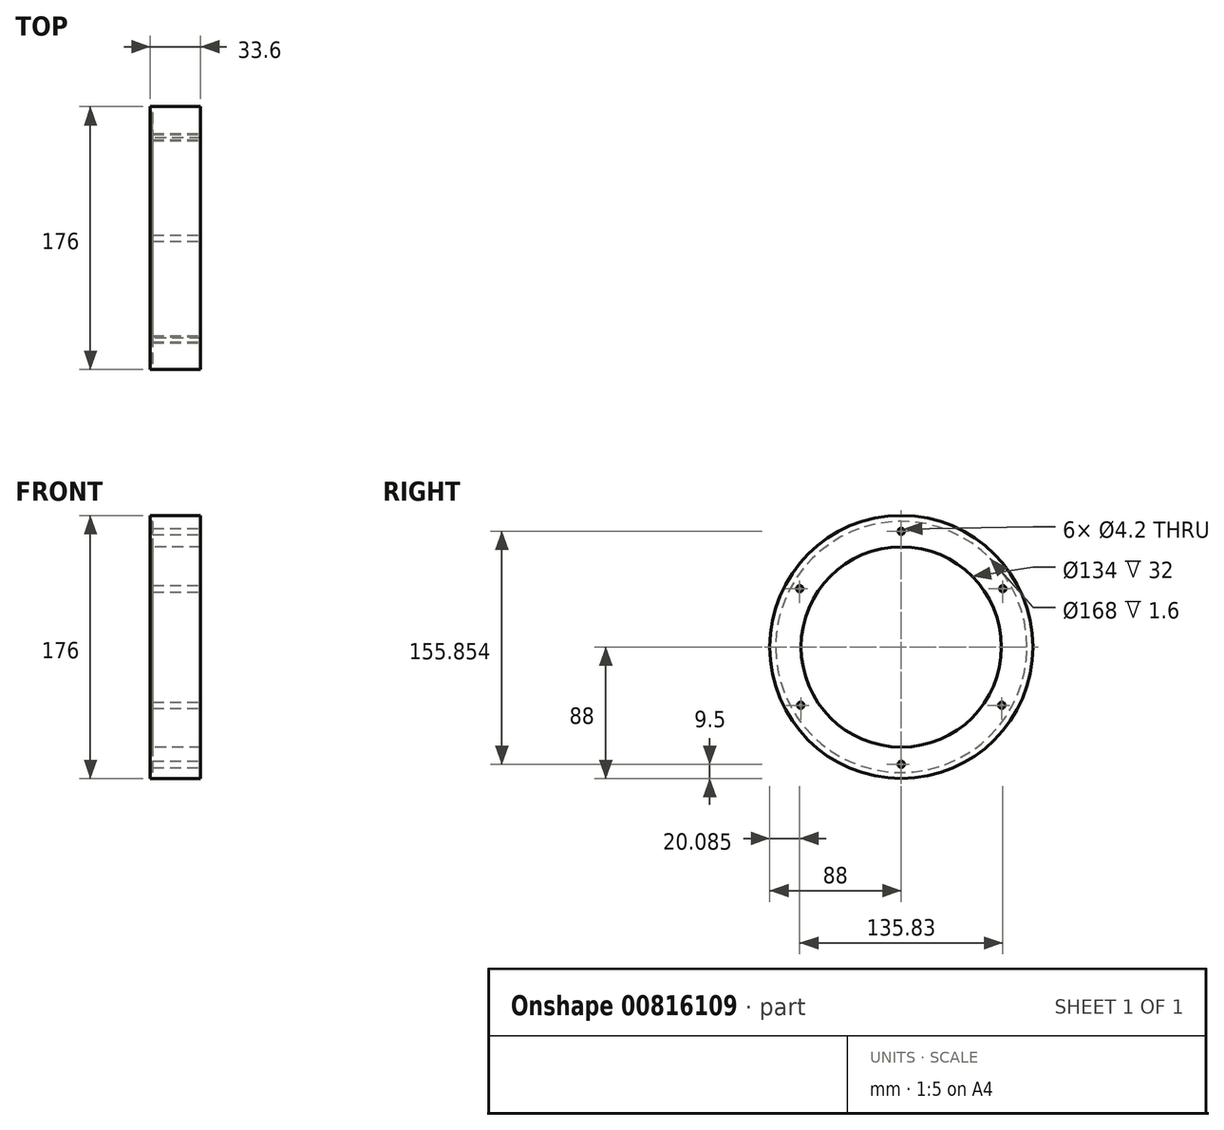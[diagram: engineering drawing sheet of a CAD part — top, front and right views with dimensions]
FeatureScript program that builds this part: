
annotation { "Feature Type Name" : "Feature", "Feature Type Description" : "" }
export const myFeature = defineFeature(function(context is Context, id is Id, definition is map)
    precondition{}
    {
        {
            var Q0;
            Q0=qCreatedBy(makeId("Front.planeOp"),FACE);
            var sketch = newSketch(context, id + "F0", { "sketchPlane" : qUnion([Q0])});
            skLineSegment(sketch, "E0", {"start": v(0, 0) * mm, "end": v(-209.58, 0) * mm, "construction": true});
            skLineSegment(sketch, "E1", {"start": v(-209.58, 0) * mm, "end": v(195.05, 0) * mm, "construction": true});
            skLineSegment(sketch, "E2", {"start": v(195.05, 0) * mm, "end": v(0, 0) * mm, "construction": true});
            skLineSegment(sketch, "E3", {"start": v(-16, 67) * mm, "end": v(16, 67) * mm});
            skLineSegment(sketch, "E4", {"start": v(16, 67) * mm, "end": v(16, 84) * mm});
            skLineSegment(sketch, "E5", {"start": v(16, 84) * mm, "end": v(16.35, 84) * mm});
            skLineSegment(sketch, "E6", {"start": v(16.35, 84) * mm, "end": v(16.35, 88) * mm});
            skLineSegment(sketch, "E7", {"start": v(16.35, 88) * mm, "end": v(-16.35, 88) * mm});
            skLineSegment(sketch, "E8", {"start": v(-16.35, 88) * mm, "end": v(-16.35, 84) * mm});
            skLineSegment(sketch, "E9", {"start": v(-16.35, 84) * mm, "end": v(-16, 84) * mm});
            skLineSegment(sketch, "E10", {"start": v(-16, 84) * mm, "end": v(-16, 67) * mm});
            skLineSegment(sketch, "E11", {"start": v(0, 0) * mm, "end": v(0, 123.2) * mm, "construction": true});
            skSolve(sketch);
        }
        {
            var Q0;
            Q0 = qSketchRegion(id + "F0", true);
            var Q1;
            Q1=sQuery(id+"F0.wireOp",EDGE,"E1");
            revolve(context, id + "F1", {"surfaceOperationType" : NewSurfaceOperationType.NEW, "entities" : qUnion([Q0]), "axis" : qUnion([Q1]), "revolveType" : RevolveType.FULL});
        }
        {
            var Q0;
            Q0=makeQuery(id+"F1.opRevolve","SWEPT_FACE",FACE,{"disambiguationData":[OSD([sQuery(id+"F0.wireOp",EDGE,"E6")])]});
            extrude(context, id + "F2", {"entities" : qUnion([Q0]), "operationType" : NewBodyOperationType.REMOVE, "oppositeDirection" : true, "depth" : 0.7 * mm, "offsetDistance" : 25 * mm});
        }
        {
            var Q0;
            Q0=makeQuery(id+"F2.boolean.opBoolean","COPY",FACE,{"derivedFrom":makeQuery(id+"F2.opExtrude","CAP_FACE",FACE,{"disambiguationData":[OSD([sQuery(id+"F0.wireOp",EDGE,"E6")])],"isStart":false})});
            extrude(context, id + "F3", {"entities" : qUnion([Q0]), "operationType" : NewBodyOperationType.ADD, "depth" : 0.35 * mm, "offsetDistance" : 25 * mm});
        }
        {
            var Q0;
            Q0=makeQuery(id+"F3.boolean.opBoolean","MERGE",FACE,{"derivedFrom":[makeQuery(id+"F1.opRevolve","SWEPT_FACE",FACE,{"disambiguationData":[OSD([sQuery(id+"F0.wireOp",EDGE,"E4")])]}),makeQuery(id+"F3.opExtrude","CAP_FACE",FACE,{"disambiguationData":[OSD([sQuery(id+"F0.wireOp",EDGE,"E6")])],"isStart":false})]});
            var sketch = newSketch(context, id + "F4", { "sketchPlane" : qUnion([Q0])});
            skPoint(sketch, "E12", {"position": v(0, 77.35) * mm});
            skPoint(sketch, "E13", {"position": v(0, -78.5) * mm});
            skPoint(sketch, "E14", {"position": v(67.26, -39) * mm});
            skPoint(sketch, "E15", {"position": v(-67.26, -39) * mm});
            skPoint(sketch, "E16", {"position": v(-67.91, 39) * mm});
            skPoint(sketch, "E17", {"position": v(67.91, 39) * mm});
            skCircle(sketch, "E18", {"center": v(0, 0) * mm, "radius": 78.23 * mm, "construction": true});
            skSolve(sketch);
        }
        {
            var Q0;
            Q0=sQuery(id+"F4.wireOp",VERTEX,"E16");
            var Q1;
            Q1=sQuery(id+"F4.wireOp",VERTEX,"E12");
            var Q2;
            Q2=sQuery(id+"F4.wireOp",VERTEX,"E17");
            var Q3;
            Q3=sQuery(id+"F4.wireOp",VERTEX,"E14");
            var Q4;
            Q4=sQuery(id+"F4.wireOp",VERTEX,"E13");
            var Q5;
            Q5=sQuery(id+"F4.wireOp",VERTEX,"E15");
            var Q6;
            Q6=makeQuery(id+"F1.opRevolve","SWEPT_BODY",BODY,{"disambiguationData":[OSD([sQuery(id+"F0.wireOp",EDGE,"E3"),sQuery(id+"F0.wireOp",EDGE,"E4"),sQuery(id+"F0.wireOp",EDGE,"E5"),sQuery(id+"F0.wireOp",EDGE,"E6"),sQuery(id+"F0.wireOp",EDGE,"E7"),sQuery(id+"F0.wireOp",EDGE,"E8"),sQuery(id+"F0.wireOp",EDGE,"E9"),sQuery(id+"F0.wireOp",EDGE,"E10")])]});
            hole(context, id + "F5", {"style" : HoleStyle.SIMPLE, "endStyle" : HoleEndStyle.THROUGH, "holeDiameter" : 4.2 * mm, "majorDiameter" : 5 * mm, "isTappedThrough" : true, "tappedDepth" : 12 * mm, "tapClearance" : 3, "locations" : qUnion([Q0, Q1, Q2, Q3, Q4, Q5]), "scope" : qUnion([Q6])});
        }
        {
            var Q0;
            Q0=makeQuery(id+"F1.opRevolve","SWEPT_FACE",FACE,{"disambiguationData":[OSD([sQuery(id+"F0.wireOp",EDGE,"E8")])]});
            extrude(context, id + "F6", {"entities" : qUnion([Q0]), "operationType" : NewBodyOperationType.ADD, "depth" : 1.25 * mm, "offsetDistance" : 25 * mm});
        }
    });
